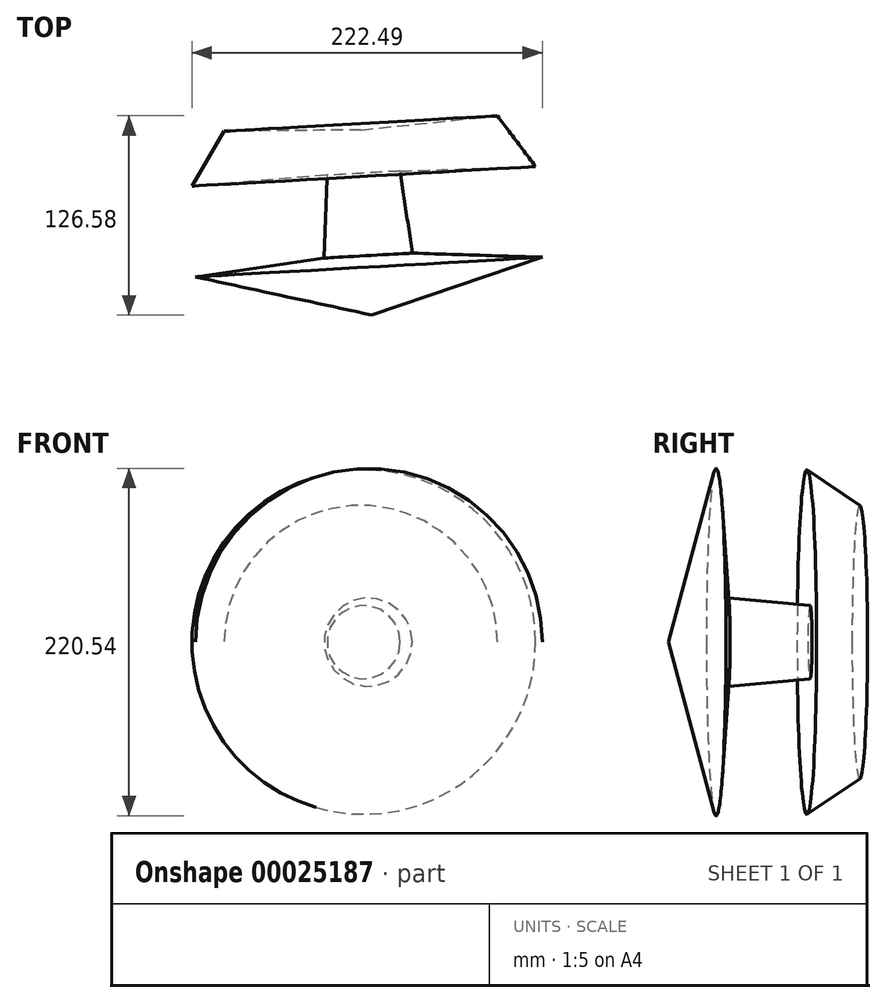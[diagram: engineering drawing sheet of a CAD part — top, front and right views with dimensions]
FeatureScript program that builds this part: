
annotation { "Feature Type Name" : "Feature", "Feature Type Description" : "" }
export const myFeature = defineFeature(function(context is Context, id is Id, definition is map)
    precondition{}
    {
        {
            var Q0;
            Q0=qCreatedBy(makeId("Top.planeOp"),FACE);
            var sketch = newSketch(context, id + "F0", { "sketchPlane" : qUnion([Q0])});
            skLineSegment(sketch, "E0", {"start": v(-30.48, 50.62) * mm, "end": v(-50.98, 15.77) * mm});
            skLineSegment(sketch, "E1", {"start": v(-50.98, 15.77) * mm, "end": v(34.81, 22.63) * mm});
            skLineSegment(sketch, "E2", {"start": v(34.81, 22.63) * mm, "end": v(33, -29.96) * mm});
            skLineSegment(sketch, "E3", {"start": v(33, -29.96) * mm, "end": v(-48.67, -41.92) * mm});
            skLineSegment(sketch, "E4", {"start": v(-48.67, -41.92) * mm, "end": v(63.15, -66.13) * mm});
            skLineSegment(sketch, "E5", {"start": v(63.15, -66.13) * mm, "end": v(56.48, 51.5) * mm});
            skLineSegment(sketch, "E6", {"start": v(56.48, 51.5) * mm, "end": v(-30.48, 50.62) * mm});
            skSolve(sketch);
        }
        {
            var Q0;
            Q0=makeQuery(id+"F0.imprint","IMPRINT",FACE,{"disambiguationData":[TD([[makeQuery(id+"F0.imprint","IMPRINT",EDGE,{"derivedFrom":sQuery(id+"F0.wireOp",EDGE,"E0")}),1.0]])]});
            var Q1;
            Q1=sQuery(id+"F0.wireOp",EDGE,"E5");
            revolve(context, id + "F1", {"entities" : qUnion([Q0]), "axis" : qUnion([Q1]), "revolveType" : RevolveType.FULL});
        }
    });
